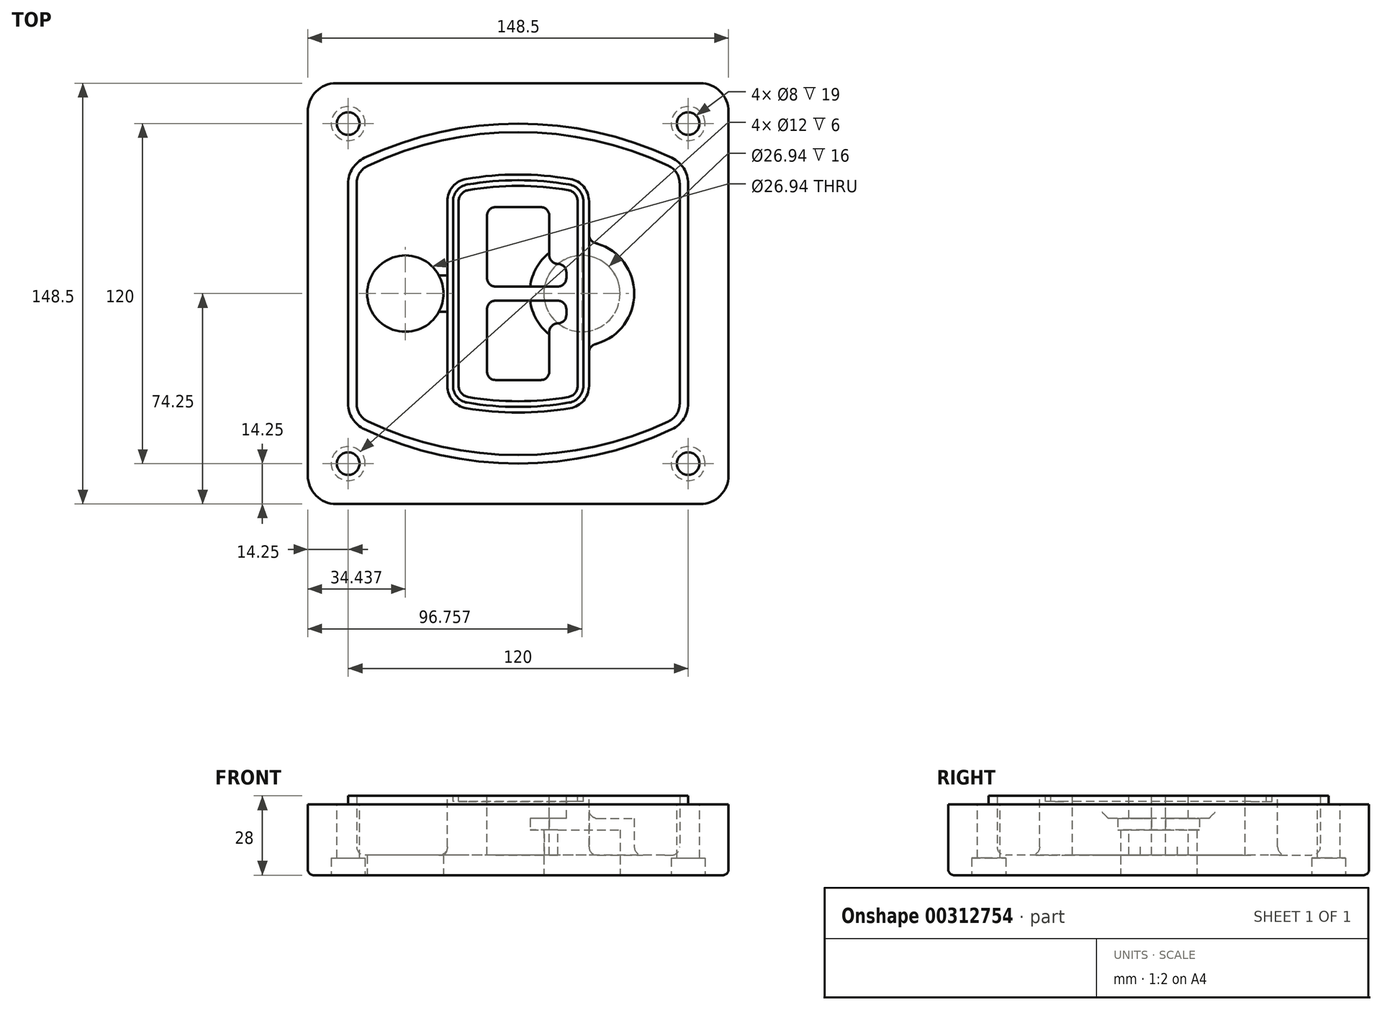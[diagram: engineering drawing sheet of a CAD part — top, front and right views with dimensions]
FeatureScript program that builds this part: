
annotation { "Feature Type Name" : "Feature", "Feature Type Description" : "" }
export const myFeature = defineFeature(function(context is Context, id is Id, definition is map)
    precondition{}
    {
        {
            var Q0;
            Q0=qCreatedBy(makeId("Top.planeOp"),FACE);
            var sketch = newSketch(context, id + "F0", { "sketchPlane" : qUnion([Q0])});
            skPoint(sketch, "E0.rect.middle", {"position": v(0, 0) * mm});
            skLineSegment(sketch, "E1.bottom", {"start": v(-64.25, -74.25) * mm, "end": v(64.25, -74.25) * mm});
            skLineSegment(sketch, "E1.top", {"start": v(-64.25, 74.25) * mm, "end": v(64.25, 74.25) * mm});
            skLineSegment(sketch, "E1.left", {"start": v(-74.25, -64.25) * mm, "end": v(-74.25, 64.25) * mm});
            skLineSegment(sketch, "E1.right", {"start": v(74.25, -64.25) * mm, "end": v(74.25, 64.25) * mm});
            skLineSegment(sketch, "E2", {"start": v(-74.25, 74.25) * mm, "end": v(74.25, -74.25) * mm, "construction": true});
            skLineSegment(sketch, "E3", {"start": v(74.25, 74.25) * mm, "end": v(-74.25, -74.25) * mm, "construction": true});
            skCircle(sketch, "E4", {"center": v(-60, 60) * mm, "radius": 4 * mm});
            skCircle(sketch, "E5", {"center": v(60, 60) * mm, "radius": 4 * mm});
            skCircle(sketch, "E6", {"center": v(60, -60) * mm, "radius": 4 * mm});
            skCircle(sketch, "E7", {"center": v(-60, -60) * mm, "radius": 4 * mm});
            skLineSegment(sketch, "E8", {"start": v(-60, 60) * mm, "end": v(60, 60) * mm, "construction": true});
            skLineSegment(sketch, "E9", {"start": v(60, 60) * mm, "end": v(60, -60) * mm, "construction": true});
            skLineSegment(sketch, "E10", {"start": v(60, -60) * mm, "end": v(-60, -60) * mm, "construction": true});
            skLineSegment(sketch, "E11", {"start": v(-60, -60) * mm, "end": v(-60, 60) * mm, "construction": true});
            skLineSegment(sketch, "E12", {"start": v(-60, 38.83) * mm, "end": v(-60, -38.83) * mm});
            skLineSegment(sketch, "E13", {"start": v(60, 38.83) * mm, "end": v(60, -38.83) * mm});
            skArc(sketch, "E14", {"start": v(54.26, 47.88) * mm, "mid": v(0, 60) * mm, "end": v(-54.26, 47.88) * mm});
            skArc(sketch, "E15", {"start": v(-54.26, -47.88) * mm, "mid": v(0, -60) * mm, "end": v(54.26, -47.88) * mm});
            skLineSegment(sketch, "E16", {"start": v(-60, 0) * mm, "end": v(60, 0) * mm, "construction": true});
            skPoint(sketch, "E17.visualSharp", {"position": v(-60, -45) * mm});
            skArc(sketch, "E17.filletArc", {"start": v(-60, -38.83) * mm, "mid": v(-58.44, -44.2) * mm, "end": v(-54.26, -47.88) * mm});
            skPoint(sketch, "E18.visualSharp", {"position": v(-60, 45) * mm});
            skArc(sketch, "E18.filletArc", {"start": v(-54.26, 47.88) * mm, "mid": v(-58.44, 44.2) * mm, "end": v(-60, 38.83) * mm});
            skPoint(sketch, "E19.visualSharp", {"position": v(60, 45) * mm});
            skArc(sketch, "E19.filletArc", {"start": v(60, 38.83) * mm, "mid": v(58.44, 44.2) * mm, "end": v(54.26, 47.88) * mm});
            skPoint(sketch, "E20.visualSharp", {"position": v(60, -45) * mm});
            skArc(sketch, "E20.filletArc", {"start": v(54.26, -47.88) * mm, "mid": v(58.44, -44.2) * mm, "end": v(60, -38.83) * mm});
            skPoint(sketch, "E21.visualSharp", {"position": v(-74.25, 74.25) * mm});
            skArc(sketch, "E21.filletArc", {"start": v(-64.25, 74.25) * mm, "mid": v(-71.32, 71.32) * mm, "end": v(-74.25, 64.25) * mm});
            skPoint(sketch, "E22.visualSharp", {"position": v(74.25, 74.25) * mm});
            skArc(sketch, "E22.filletArc", {"start": v(74.25, 64.25) * mm, "mid": v(71.32, 71.32) * mm, "end": v(64.25, 74.25) * mm});
            skPoint(sketch, "E23.visualSharp", {"position": v(74.25, -74.25) * mm});
            skArc(sketch, "E23.filletArc", {"start": v(64.25, -74.25) * mm, "mid": v(71.32, -71.32) * mm, "end": v(74.25, -64.25) * mm});
            skPoint(sketch, "E24.visualSharp", {"position": v(-74.25, -74.25) * mm});
            skArc(sketch, "E24.filletArc", {"start": v(-74.25, -64.25) * mm, "mid": v(-71.32, -71.32) * mm, "end": v(-64.25, -74.25) * mm});
            skArc(sketch, "E25.0", {"start": v(57, 38.83) * mm, "mid": v(55.9, 42.58) * mm, "end": v(52.98, 45.17) * mm});
            skLineSegment(sketch, "E25.1", {"start": v(57, 38.83) * mm, "end": v(57, -38.83) * mm});
            skArc(sketch, "E25.2", {"start": v(52.98, -45.17) * mm, "mid": v(55.9, -42.58) * mm, "end": v(57, -38.83) * mm});
            skArc(sketch, "E25.3", {"start": v(-52.98, -45.17) * mm, "mid": v(0, -57) * mm, "end": v(52.98, -45.17) * mm});
            skArc(sketch, "E25.4", {"start": v(-57, -38.83) * mm, "mid": v(-55.9, -42.58) * mm, "end": v(-52.98, -45.17) * mm});
            skArc(sketch, "E25.5", {"start": v(52.98, 45.17) * mm, "mid": v(0, 57) * mm, "end": v(-52.98, 45.17) * mm});
            skLineSegment(sketch, "E25.6", {"start": v(-57, 38.83) * mm, "end": v(-57, -38.83) * mm});
            skArc(sketch, "E25.7", {"start": v(-52.98, 45.17) * mm, "mid": v(-55.9, 42.58) * mm, "end": v(-57, 38.83) * mm});
            skArc(sketch, "E26.0", {"start": v(-55.96, 51.5) * mm, "mid": v(-61.82, 46.33) * mm, "end": v(-64, 38.83) * mm});
            skArc(sketch, "E26.1", {"start": v(55.96, 51.5) * mm, "mid": v(0, 64) * mm, "end": v(-55.96, 51.5) * mm});
            skArc(sketch, "E26.2", {"start": v(64, 38.83) * mm, "mid": v(61.82, 46.33) * mm, "end": v(55.96, 51.5) * mm});
            skLineSegment(sketch, "E26.3", {"start": v(64, 38.83) * mm, "end": v(64, -38.83) * mm});
            skArc(sketch, "E26.4", {"start": v(55.96, -51.5) * mm, "mid": v(61.82, -46.33) * mm, "end": v(64, -38.83) * mm});
            skLineSegment(sketch, "E26.5", {"start": v(-64, 38.83) * mm, "end": v(-64, -38.83) * mm});
            skArc(sketch, "E26.6", {"start": v(-55.96, -51.5) * mm, "mid": v(0, -64) * mm, "end": v(55.96, -51.5) * mm});
            skArc(sketch, "E26.7", {"start": v(-64, -38.83) * mm, "mid": v(-61.82, -46.33) * mm, "end": v(-55.96, -51.5) * mm});
            skLineSegment(sketch, "E27", {"start": v(0, 74.25) * mm, "end": v(0, 104.25) * mm, "construction": true});
            skPoint(sketch, "E27.endSnap0", {"position": v(0, 74.25) * mm});
            skCircle(sketch, "E28", {"center": v(0, 104.25) * mm, "radius": 0.06 * mm});
            skCircle(sketch, "E29", {"center": v(0, 104.25) * mm, "radius": 6 * mm});
            skLineSegment(sketch, "E30", {"start": v(-42.56, 74.25) * mm, "end": v(-18.11, 96.1) * mm});
            skLineSegment(sketch, "E31", {"start": v(11.89, 96.1) * mm, "end": v(31.43, 74.25) * mm});
            skLineSegment(sketch, "E32", {"start": v(-18.11, 96.1) * mm, "end": v(-18.11, 113.16) * mm});
            skLineSegment(sketch, "E33", {"start": v(11.89, 96.1) * mm, "end": v(11.89, 113.16) * mm});
            skArc(sketch, "E34", {"start": v(11.89, 113.16) * mm, "mid": v(-3.11, 128.16) * mm, "end": v(-18.11, 113.16) * mm});
            skSolve(sketch);
        }
        {
            var Q0;
            Q0=makeQuery(id+"F0.imprint","IMPRINT",FACE,{"disambiguationData":[TD([[makeQuery(id+"F0.imprint","IMPRINT",EDGE,{"derivedFrom":sQuery(id+"F0.wireOp",EDGE,"E1.bottom")}),1.0]])]});
            var Q1;
            Q1=makeQuery(id+"F0.imprint","IMPRINT",FACE,{"disambiguationData":[TD([[makeQuery(id+"F0.imprint","IMPRINT",EDGE,{"derivedFrom":sQuery(id+"F0.wireOp",EDGE,"E12")}),1.0]])]});
            var Q2;
            Q2=makeQuery(id+"F0.imprint","IMPRINT",FACE,{"disambiguationData":[TD([[makeQuery(id+"F0.imprint","IMPRINT",EDGE,{"derivedFrom":sQuery(id+"F0.wireOp",EDGE,"E25.0")}),1.0]])]});
            var Q3;
            Q3=makeQuery(id+"F0.imprint","IMPRINT",FACE,{"disambiguationData":[TD([[makeQuery(id+"F0.imprint","IMPRINT",EDGE,{"derivedFrom":sQuery(id+"F0.wireOp",EDGE,"E12")}),-1.0]])]});
            extrude(context, id + "F1", {"entities" : qUnion([Q0, Q1, Q2, Q3]), "oppositeDirection" : true, "depth" : 25 * mm});
        }
        {
            var Q0;
            Q0=makeQuery(id+"F0.imprint","IMPRINT",FACE,{"disambiguationData":[TD([[makeQuery(id+"F0.imprint","IMPRINT",EDGE,{"derivedFrom":sQuery(id+"F0.wireOp",EDGE,"E12")}),1.0]])]});
            extrude(context, id + "F2", {"entities" : qUnion([Q0]), "operationType" : NewBodyOperationType.ADD, "depth" : 3 * mm});
        }
        {
            var Q0;
            Q0=makeQuery(id+"F0.imprint","IMPRINT",FACE,{"disambiguationData":[TD([[makeQuery(id+"F0.imprint","IMPRINT",EDGE,{"derivedFrom":sQuery(id+"F0.wireOp",EDGE,"E25.0")}),1.0]])]});
            extrude(context, id + "F3", {"entities" : qUnion([Q0]), "operationType" : NewBodyOperationType.REMOVE, "oppositeDirection" : true, "depth" : 18 * mm});
        }
        {
            var Q0;
            Q0=makeQuery(id+"F2.opExtrude","CAP_FACE",FACE,{"disambiguationData":[OSD([sQuery(id+"F0.wireOp",EDGE,"E12"),sQuery(id+"F0.wireOp",EDGE,"E13"),sQuery(id+"F0.wireOp",EDGE,"E14"),sQuery(id+"F0.wireOp",EDGE,"E15"),sQuery(id+"F0.wireOp",EDGE,"E17.filletArc"),sQuery(id+"F0.wireOp",EDGE,"E18.filletArc"),sQuery(id+"F0.wireOp",EDGE,"E19.filletArc"),sQuery(id+"F0.wireOp",EDGE,"E20.filletArc"),sQuery(id+"F0.wireOp",EDGE,"E25.0"),sQuery(id+"F0.wireOp",EDGE,"E25.1"),sQuery(id+"F0.wireOp",EDGE,"E25.2"),sQuery(id+"F0.wireOp",EDGE,"E25.3"),sQuery(id+"F0.wireOp",EDGE,"E25.4"),sQuery(id+"F0.wireOp",EDGE,"E25.5"),sQuery(id+"F0.wireOp",EDGE,"E25.6"),sQuery(id+"F0.wireOp",EDGE,"E25.7")])],"isStart":false});
            var sketch = newSketch(context, id + "F4", { "sketchPlane" : qUnion([Q0])});
            skArc(sketch, "E35.0", {"start": v(-18.34, -40.45) * mm, "mid": v(0, -42) * mm, "end": v(18.34, -40.45) * mm});
            skArc(sketch, "E36.0", {"start": v(18.34, 40.45) * mm, "mid": v(0, 42) * mm, "end": v(-18.34, 40.45) * mm});
            skLineSegment(sketch, "E37", {"start": v(-25, 32.57) * mm, "end": v(-25, -32.57) * mm});
            skLineSegment(sketch, "E38", {"start": v(25, 32.57) * mm, "end": v(25, -32.57) * mm});
            skLineSegment(sketch, "E39", {"start": v(-25, 39.1) * mm, "end": v(25, 39.1) * mm, "construction": true});
            skLineSegment(sketch, "E40", {"start": v(-25, -39.1) * mm, "end": v(25, -39.1) * mm, "construction": true});
            skPoint(sketch, "E41.visualSharp", {"position": v(-25, 39.1) * mm});
            skArc(sketch, "E41.filletArc", {"start": v(-18.34, 40.45) * mm, "mid": v(-23.11, 37.73) * mm, "end": v(-25, 32.57) * mm});
            skPoint(sketch, "E42.visualSharp", {"position": v(25, 39.1) * mm});
            skArc(sketch, "E42.filletArc", {"start": v(25, 32.57) * mm, "mid": v(23.11, 37.73) * mm, "end": v(18.34, 40.45) * mm});
            skPoint(sketch, "E43.visualSharp", {"position": v(25, -39.1) * mm});
            skArc(sketch, "E43.filletArc", {"start": v(18.34, -40.45) * mm, "mid": v(23.11, -37.73) * mm, "end": v(25, -32.57) * mm});
            skPoint(sketch, "E44.visualSharp", {"position": v(-25, -39.1) * mm});
            skArc(sketch, "E44.filletArc", {"start": v(-25, -32.57) * mm, "mid": v(-23.11, -37.73) * mm, "end": v(-18.34, -40.45) * mm});
            skArc(sketch, "E45.0", {"start": v(52.98, 45.17) * mm, "mid": v(0, 57) * mm, "end": v(-52.98, 45.17) * mm});
            skArc(sketch, "E45.1", {"start": v(-52.98, 45.17) * mm, "mid": v(-55.9, 42.58) * mm, "end": v(-57, 38.83) * mm});
            skLineSegment(sketch, "E45.2", {"start": v(-57, 38.83) * mm, "end": v(-57, -38.83) * mm});
            skArc(sketch, "E45.3", {"start": v(-57, -38.83) * mm, "mid": v(-55.9, -42.58) * mm, "end": v(-52.98, -45.17) * mm});
            skArc(sketch, "E45.4", {"start": v(-52.98, -45.17) * mm, "mid": v(0, -57) * mm, "end": v(52.98, -45.17) * mm});
            skArc(sketch, "E45.5", {"start": v(52.98, -45.17) * mm, "mid": v(55.9, -42.58) * mm, "end": v(57, -38.83) * mm});
            skLineSegment(sketch, "E45.6", {"start": v(57, 38.83) * mm, "end": v(57, -38.83) * mm});
            skArc(sketch, "E45.7", {"start": v(57, 38.83) * mm, "mid": v(55.9, 42.58) * mm, "end": v(52.98, 45.17) * mm});
            skLineSegment(sketch, "E46.0", {"start": v(23, 32.57) * mm, "end": v(23, -32.57) * mm});
            skArc(sketch, "E46.1", {"start": v(18, -38.48) * mm, "mid": v(21.58, -36.44) * mm, "end": v(23, -32.57) * mm});
            skArc(sketch, "E46.2", {"start": v(-18, -38.48) * mm, "mid": v(0, -40) * mm, "end": v(18, -38.48) * mm});
            skArc(sketch, "E46.3", {"start": v(-23, -32.57) * mm, "mid": v(-21.58, -36.44) * mm, "end": v(-18, -38.48) * mm});
            skLineSegment(sketch, "E46.4", {"start": v(-23, 32.57) * mm, "end": v(-23, -32.57) * mm});
            skArc(sketch, "E46.5", {"start": v(23, 32.57) * mm, "mid": v(21.58, 36.44) * mm, "end": v(18, 38.48) * mm});
            skArc(sketch, "E46.6", {"start": v(-18, 38.48) * mm, "mid": v(-21.58, 36.44) * mm, "end": v(-23, 32.57) * mm});
            skArc(sketch, "E46.7", {"start": v(18, 38.48) * mm, "mid": v(0, 40) * mm, "end": v(-18, 38.48) * mm});
            skArc(sketch, "E47.0", {"start": v(21, 32.57) * mm, "mid": v(20.06, 35.15) * mm, "end": v(17.67, 36.5) * mm});
            skLineSegment(sketch, "E47.1", {"start": v(21, 32.57) * mm, "end": v(21, -32.57) * mm});
            skArc(sketch, "E47.2", {"start": v(17.67, -36.5) * mm, "mid": v(20.06, -35.15) * mm, "end": v(21, -32.57) * mm});
            skArc(sketch, "E47.3", {"start": v(-17.67, -36.5) * mm, "mid": v(0, -38) * mm, "end": v(17.67, -36.5) * mm});
            skArc(sketch, "E47.4", {"start": v(-21, -32.57) * mm, "mid": v(-20.06, -35.15) * mm, "end": v(-17.67, -36.5) * mm});
            skArc(sketch, "E47.5", {"start": v(17.67, 36.5) * mm, "mid": v(0, 38) * mm, "end": v(-17.67, 36.5) * mm});
            skLineSegment(sketch, "E47.6", {"start": v(-21, 32.57) * mm, "end": v(-21, -32.57) * mm});
            skArc(sketch, "E47.7", {"start": v(-17.67, 36.5) * mm, "mid": v(-20.06, 35.15) * mm, "end": v(-21, 32.57) * mm});
            skLineSegment(sketch, "E48", {"start": v(-25, 0) * mm, "end": v(25, 0) * mm, "construction": true});
            skLineSegment(sketch, "E49", {"start": v(-11, 5.5) * mm, "end": v(-11, 27.5) * mm});
            skLineSegment(sketch, "E50", {"start": v(-8, 30.5) * mm, "end": v(8, 30.5) * mm});
            skLineSegment(sketch, "E51", {"start": v(11, 27.5) * mm, "end": v(11, 13.5) * mm});
            skLineSegment(sketch, "E52", {"start": v(14, 10.5) * mm, "end": v(14, 10.5) * mm});
            skLineSegment(sketch, "E53", {"start": v(17, 7.5) * mm, "end": v(17, 5.5) * mm});
            skLineSegment(sketch, "E54", {"start": v(14, 2.5) * mm, "end": v(-8, 2.5) * mm});
            skPoint(sketch, "E55.visualSharp", {"position": v(-11, 30.5) * mm});
            skArc(sketch, "E55.filletArc", {"start": v(-8, 30.5) * mm, "mid": v(-10.12, 29.62) * mm, "end": v(-11, 27.5) * mm});
            skPoint(sketch, "E56.visualSharp", {"position": v(11, 30.5) * mm});
            skArc(sketch, "E56.filletArc", {"start": v(11, 27.5) * mm, "mid": v(10.12, 29.62) * mm, "end": v(8, 30.5) * mm});
            skPoint(sketch, "E57.visualSharp", {"position": v(11, 10.5) * mm});
            skArc(sketch, "E57.filletArc", {"start": v(11, 13.5) * mm, "mid": v(11.88, 11.38) * mm, "end": v(14, 10.5) * mm});
            skPoint(sketch, "E58.visualSharp", {"position": v(17, 10.5) * mm});
            skArc(sketch, "E58.filletArc", {"start": v(17, 7.5) * mm, "mid": v(16.12, 9.62) * mm, "end": v(14, 10.5) * mm});
            skPoint(sketch, "E59.visualSharp", {"position": v(17, 2.5) * mm});
            skArc(sketch, "E59.filletArc", {"start": v(14, 2.5) * mm, "mid": v(16.12, 3.38) * mm, "end": v(17, 5.5) * mm});
            skPoint(sketch, "E60.visualSharp", {"position": v(-11, 2.5) * mm});
            skArc(sketch, "E60.filletArc", {"start": v(-11, 5.5) * mm, "mid": v(-10.12, 3.38) * mm, "end": v(-8, 2.5) * mm});
            skLineSegment(sketch, "E61.0.MirrorCS", {"start": v(14, -2.5) * mm, "end": v(-8, -2.5) * mm});
            skArc(sketch, "E62.0.MirrorCS", {"start": v(-11, -5.5) * mm, "mid": v(-10.12, -3.38) * mm, "end": v(-8, -2.5) * mm});
            skLineSegment(sketch, "E63.0.MirrorCS", {"start": v(-11, -5.5) * mm, "end": v(-11, -27.5) * mm});
            skArc(sketch, "E64.0.MirrorCS", {"start": v(-8, -30.5) * mm, "mid": v(-10.12, -29.62) * mm, "end": v(-11, -27.5) * mm});
            skLineSegment(sketch, "E65.0.MirrorCS", {"start": v(-8, -30.5) * mm, "end": v(8, -30.5) * mm});
            skArc(sketch, "E66.0.MirrorCS", {"start": v(11, -27.5) * mm, "mid": v(10.12, -29.62) * mm, "end": v(8, -30.5) * mm});
            skLineSegment(sketch, "E67.0.MirrorCS", {"start": v(11, -27.5) * mm, "end": v(11, -13.5) * mm});
            skArc(sketch, "E68.0.MirrorCS", {"start": v(11, -13.5) * mm, "mid": v(11.88, -11.38) * mm, "end": v(14, -10.5) * mm});
            skArc(sketch, "E69.0.MirrorCS", {"start": v(17, -7.5) * mm, "mid": v(16.12, -9.62) * mm, "end": v(14, -10.5) * mm});
            skLineSegment(sketch, "E70.0.MirrorCS", {"start": v(17, -7.5) * mm, "end": v(17, -5.5) * mm});
            skArc(sketch, "E71.0.MirrorCS", {"start": v(14, -2.5) * mm, "mid": v(16.12, -3.38) * mm, "end": v(17, -5.5) * mm});
            skSolve(sketch);
        }
        {
            var Q0;
            Q0=makeQuery(id+"F4.imprint","IMPRINT",FACE,{"disambiguationData":[TD([[makeQuery(id+"F4.imprint","IMPRINT",EDGE,{"derivedFrom":sQuery(id+"F4.wireOp",EDGE,"E35.0")}),1.0]])]});
            var Q1;
            Q1=makeQuery(id+"F4.imprint","IMPRINT",FACE,{"disambiguationData":[TD([[makeQuery(id+"F4.imprint","IMPRINT",EDGE,{"derivedFrom":sQuery(id+"F4.wireOp",EDGE,"E46.0")}),-1.0]])]});
            var Q2;
            Q2=makeQuery(id+"F4.imprint","IMPRINT",FACE,{"disambiguationData":[TD([[makeQuery(id+"F4.imprint","IMPRINT",EDGE,{"derivedFrom":sQuery(id+"F4.wireOp",EDGE,"E47.0")}),1.0]])]});
            extrude(context, id + "F5", {"entities" : qUnion([Q0, Q1, Q2]), "operationType" : NewBodyOperationType.ADD, "endBound" : BoundingType.UP_TO_NEXT, "oppositeDirection" : true, "depth" : 25 * mm});
        }
        {
            var Q0;
            Q0=makeQuery(id+"F4.imprint","IMPRINT",FACE,{"disambiguationData":[TD([[makeQuery(id+"F4.imprint","IMPRINT",EDGE,{"derivedFrom":sQuery(id+"F4.wireOp",EDGE,"E46.0")}),-1.0]])]});
            extrude(context, id + "F6", {"entities" : qUnion([Q0]), "operationType" : NewBodyOperationType.REMOVE, "oppositeDirection" : true, "depth" : 2 * mm});
        }
        {
            var Q0;
            Q0=makeQuery(id+"F1.opExtrude","CAP_FACE",FACE,{"disambiguationData":[OSD([sQuery(id+"F0.wireOp",EDGE,"E1.bottom"),sQuery(id+"F0.wireOp",EDGE,"E1.top"),sQuery(id+"F0.wireOp",EDGE,"E1.left"),sQuery(id+"F0.wireOp",EDGE,"E1.right"),sQuery(id+"F0.wireOp",EDGE,"E4"),sQuery(id+"F0.wireOp",EDGE,"E5"),sQuery(id+"F0.wireOp",EDGE,"E6"),sQuery(id+"F0.wireOp",EDGE,"E7"),sQuery(id+"F0.wireOp",EDGE,"E21.filletArc"),sQuery(id+"F0.wireOp",EDGE,"E22.filletArc"),sQuery(id+"F0.wireOp",EDGE,"E23.filletArc"),sQuery(id+"F0.wireOp",EDGE,"E24.filletArc")])],"isStart":false});
            var sketch = newSketch(context, id + "F7", { "sketchPlane" : qUnion([Q0])});
            skCircle(sketch, "E72", {"center": v(22.5, 0) * mm, "radius": 13.47 * mm});
            skCircle(sketch, "E73", {"center": v(-39.81, 0) * mm, "radius": 13.47 * mm});
            skLineSegment(sketch, "E74", {"start": v(74.25, 0) * mm, "end": v(-74.25, 0) * mm});
            skCircle(sketch, "E75", {"center": v(22.5, 0) * mm, "radius": 18.47 * mm});
            skCircle(sketch, "E76", {"center": v(60, -60) * mm, "radius": 6 * mm});
            skCircle(sketch, "E77", {"center": v(-60, -60) * mm, "radius": 6 * mm});
            skCircle(sketch, "E78", {"center": v(-60, 60) * mm, "radius": 6 * mm});
            skCircle(sketch, "E79", {"center": v(60, 60) * mm, "radius": 6 * mm});
            skSolve(sketch);
        }
        {
            var Q0;
            {var subQ1=sQuery(id+"F7.wireOp",EDGE,"E74");var subQ4=sQuery(id+"F7.wireOp",EDGE,"E72");var subQ6=makeQuery(id+"F7.imprint","INTERSECT",VERTEX,{"disambiguationData":[OD(0.0)],"derivedFrom":[subQ4,subQ1]});Q0=makeQuery(id+"F7.imprint","IMPRINT",FACE,{"disambiguationData":[TD([[makeQuery(id+"F7.imprint","IMPRINT",EDGE,{"disambiguationData":[TD([[subQ6,-1.0]])],"derivedFrom":subQ4}),-1.0]])]});}
            var Q1;
            {var subQ0=sQuery(id+"F7.wireOp",EDGE,"E74");var subQ1=sQuery(id+"F7.wireOp",EDGE,"E72");var subQ3=makeQuery(id+"F7.imprint","INTERSECT",VERTEX,{"disambiguationData":[OD(0.0)],"derivedFrom":[subQ1,subQ0]});Q1=makeQuery(id+"F7.imprint","IMPRINT",FACE,{"disambiguationData":[TD([[makeQuery(id+"F7.imprint","IMPRINT",EDGE,{"disambiguationData":[TD([[subQ3,-1.0]])],"derivedFrom":subQ1}),1.0]])]});}
            var Q2;
            {var subQ0=sQuery(id+"F7.wireOp",EDGE,"E74");var subQ1=sQuery(id+"F7.wireOp",EDGE,"E72");var subQ3=makeQuery(id+"F7.imprint","INTERSECT",VERTEX,{"disambiguationData":[OD(0.0)],"derivedFrom":[subQ1,subQ0]});Q2=makeQuery(id+"F7.imprint","IMPRINT",FACE,{"disambiguationData":[TD([[makeQuery(id+"F7.imprint","IMPRINT",EDGE,{"disambiguationData":[TD([[subQ3,1.0]])],"derivedFrom":subQ1}),1.0]])]});}
            var Q3;
            {var subQ1=sQuery(id+"F7.wireOp",EDGE,"E74");var subQ4=sQuery(id+"F7.wireOp",EDGE,"E72");var subQ6=makeQuery(id+"F7.imprint","INTERSECT",VERTEX,{"disambiguationData":[OD(0.0)],"derivedFrom":[subQ4,subQ1]});Q3=makeQuery(id+"F7.imprint","IMPRINT",FACE,{"disambiguationData":[TD([[makeQuery(id+"F7.imprint","IMPRINT",EDGE,{"disambiguationData":[TD([[subQ6,1.0]])],"derivedFrom":subQ4}),-1.0]])]});}
            extrude(context, id + "F8", {"entities" : qUnion([Q0, Q1, Q2, Q3]), "operationType" : NewBodyOperationType.ADD, "oppositeDirection" : true, "depth" : 20 * mm});
        }
        {
            var Q0;
            {var subQ0=sQuery(id+"F7.wireOp",EDGE,"E74");var subQ1=sQuery(id+"F7.wireOp",EDGE,"E72");var subQ3=makeQuery(id+"F7.imprint","INTERSECT",VERTEX,{"disambiguationData":[OD(0.0)],"derivedFrom":[subQ1,subQ0]});Q0=makeQuery(id+"F7.imprint","IMPRINT",FACE,{"disambiguationData":[TD([[makeQuery(id+"F7.imprint","IMPRINT",EDGE,{"disambiguationData":[TD([[subQ3,-1.0]])],"derivedFrom":subQ1}),1.0]])]});}
            var Q1;
            {var subQ0=sQuery(id+"F7.wireOp",EDGE,"E74");var subQ1=sQuery(id+"F7.wireOp",EDGE,"E72");var subQ3=makeQuery(id+"F7.imprint","INTERSECT",VERTEX,{"disambiguationData":[OD(0.0)],"derivedFrom":[subQ1,subQ0]});Q1=makeQuery(id+"F7.imprint","IMPRINT",FACE,{"disambiguationData":[TD([[makeQuery(id+"F7.imprint","IMPRINT",EDGE,{"disambiguationData":[TD([[subQ3,1.0]])],"derivedFrom":subQ1}),1.0]])]});}
            extrude(context, id + "F9", {"entities" : qUnion([Q0, Q1]), "operationType" : NewBodyOperationType.REMOVE, "oppositeDirection" : true, "depth" : 16 * mm});
        }
        {
            var Q0;
            {var subQ0=sQuery(id+"F7.wireOp",EDGE,"E74");var subQ1=sQuery(id+"F7.wireOp",EDGE,"E73");var subQ3=makeQuery(id+"F7.imprint","INTERSECT",VERTEX,{"disambiguationData":[OD(0.0)],"derivedFrom":[subQ1,subQ0]});Q0=makeQuery(id+"F7.imprint","IMPRINT",FACE,{"disambiguationData":[TD([[makeQuery(id+"F7.imprint","IMPRINT",EDGE,{"disambiguationData":[TD([[subQ3,-1.0]])],"derivedFrom":subQ1}),1.0]])]});}
            var Q1;
            {var subQ0=sQuery(id+"F7.wireOp",EDGE,"E74");var subQ1=sQuery(id+"F7.wireOp",EDGE,"E73");var subQ3=makeQuery(id+"F7.imprint","INTERSECT",VERTEX,{"disambiguationData":[OD(0.0)],"derivedFrom":[subQ1,subQ0]});Q1=makeQuery(id+"F7.imprint","IMPRINT",FACE,{"disambiguationData":[TD([[makeQuery(id+"F7.imprint","IMPRINT",EDGE,{"disambiguationData":[TD([[subQ3,1.0]])],"derivedFrom":subQ1}),1.0]])]});}
            extrude(context, id + "F10", {"entities" : qUnion([Q0, Q1]), "operationType" : NewBodyOperationType.REMOVE, "oppositeDirection" : true, "depth" : 25 * mm});
        }
        {
            var Q0;
            Q0=makeQuery(id+"F7.imprint","IMPRINT",FACE,{"disambiguationData":[TD([[makeQuery(id+"F7.imprint","IMPRINT",EDGE,{"derivedFrom":sQuery(id+"F7.wireOp",EDGE,"E76")}),1.0]])]});
            var Q1;
            Q1=makeQuery(id+"F7.imprint","IMPRINT",FACE,{"disambiguationData":[TD([[makeQuery(id+"F7.imprint","IMPRINT",EDGE,{"derivedFrom":makeQuery(id+"F1.opExtrude","CAP_EDGE",EDGE,{"disambiguationData":[OSD([sQuery(id+"F0.wireOp",EDGE,"E5")])],"isStart":false})}),-1.0]])]});
            var Q2;
            Q2=makeQuery(id+"F7.imprint","IMPRINT",FACE,{"disambiguationData":[TD([[makeQuery(id+"F7.imprint","IMPRINT",EDGE,{"derivedFrom":sQuery(id+"F7.wireOp",EDGE,"E77")}),1.0]])]});
            var Q3;
            Q3=makeQuery(id+"F7.imprint","IMPRINT",FACE,{"disambiguationData":[TD([[makeQuery(id+"F7.imprint","IMPRINT",EDGE,{"derivedFrom":makeQuery(id+"F1.opExtrude","CAP_EDGE",EDGE,{"disambiguationData":[OSD([sQuery(id+"F0.wireOp",EDGE,"E4")])],"isStart":false})}),-1.0]])]});
            var Q4;
            Q4=makeQuery(id+"F7.imprint","IMPRINT",FACE,{"disambiguationData":[TD([[makeQuery(id+"F7.imprint","IMPRINT",EDGE,{"derivedFrom":sQuery(id+"F7.wireOp",EDGE,"E78")}),1.0]])]});
            var Q5;
            Q5=makeQuery(id+"F7.imprint","IMPRINT",FACE,{"disambiguationData":[TD([[makeQuery(id+"F7.imprint","IMPRINT",EDGE,{"derivedFrom":makeQuery(id+"F1.opExtrude","CAP_EDGE",EDGE,{"disambiguationData":[OSD([sQuery(id+"F0.wireOp",EDGE,"E7")])],"isStart":false})}),-1.0]])]});
            var Q6;
            Q6=makeQuery(id+"F7.imprint","IMPRINT",FACE,{"disambiguationData":[TD([[makeQuery(id+"F7.imprint","IMPRINT",EDGE,{"derivedFrom":sQuery(id+"F7.wireOp",EDGE,"E79")}),1.0]])]});
            var Q7;
            Q7=makeQuery(id+"F7.imprint","IMPRINT",FACE,{"disambiguationData":[TD([[makeQuery(id+"F7.imprint","IMPRINT",EDGE,{"derivedFrom":makeQuery(id+"F1.opExtrude","CAP_EDGE",EDGE,{"disambiguationData":[OSD([sQuery(id+"F0.wireOp",EDGE,"E6")])],"isStart":false})}),-1.0]])]});
            extrude(context, id + "F11", {"entities" : qUnion([Q0, Q1, Q2, Q3, Q4, Q5, Q6, Q7]), "operationType" : NewBodyOperationType.REMOVE, "oppositeDirection" : true, "depth" : 6 * mm});
        }
        {
            var Q0;
            Q0=makeQuery(id+"F9.boolean.opBoolean","COPY",FACE,{"derivedFrom":makeQuery(id+"F9.opExtrude","CAP_FACE",FACE,{"disambiguationData":[OSD([sQuery(id+"F7.wireOp",EDGE,"E72")])],"isStart":false})});
            var sketch = newSketch(context, id + "F12", { "sketchPlane" : qUnion([Q0])});
            skArc(sketch, "E80.0", {"start": v(11, 14.45) * mm, "mid": v(6.45, 9.13) * mm, "end": v(4.2, 2.5) * mm});
            skArc(sketch, "E80.1", {"start": v(4.2, -2.5) * mm, "mid": v(6.45, -9.13) * mm, "end": v(11, -14.45) * mm});
            skLineSegment(sketch, "E81", {"start": v(4.2, -2.5) * mm, "end": v(14, -2.5) * mm});
            skLineSegment(sketch, "E82.0", {"start": v(14, 2.5) * mm, "end": v(4.2, 2.5) * mm});
            skArc(sketch, "E82.1", {"start": v(14, 2.5) * mm, "mid": v(16.12, 3.38) * mm, "end": v(17, 5.5) * mm});
            skLineSegment(sketch, "E82.2", {"start": v(17, 7.5) * mm, "end": v(17, 5.5) * mm});
            skArc(sketch, "E82.3", {"start": v(17, 7.5) * mm, "mid": v(16.12, 9.62) * mm, "end": v(14, 10.5) * mm});
            skArc(sketch, "E82.4", {"start": v(11, 13.5) * mm, "mid": v(11.88, 11.38) * mm, "end": v(14, 10.5) * mm});
            skLineSegment(sketch, "E82.5", {"start": v(11, 14.45) * mm, "end": v(11, 13.5) * mm});
            skLineSegment(sketch, "E82.7", {"start": v(14, -2.5) * mm, "end": v(4.2, -2.5) * mm});
            skArc(sketch, "E82.8", {"start": v(14, -2.5) * mm, "mid": v(16.12, -3.38) * mm, "end": v(17, -5.5) * mm});
            skLineSegment(sketch, "E82.9", {"start": v(17, -7.5) * mm, "end": v(17, -5.5) * mm});
            skArc(sketch, "E82.10", {"start": v(17, -7.5) * mm, "mid": v(16.12, -9.62) * mm, "end": v(14, -10.5) * mm});
            skArc(sketch, "E82.11", {"start": v(11, -13.5) * mm, "mid": v(11.88, -11.38) * mm, "end": v(14, -10.5) * mm});
            skLineSegment(sketch, "E82.12", {"start": v(11, -14.45) * mm, "end": v(11, -13.5) * mm});
            skPoint(sketch, "E83.orphan", {"position": v(11, -27.5) * mm});
            skPoint(sketch, "E84.orphan", {"position": v(-8, -2.5) * mm});
            skPoint(sketch, "E85.orphan", {"position": v(-8, 2.5) * mm});
            skPoint(sketch, "E86.orphan", {"position": v(11, 27.5) * mm});
            skSolve(sketch);
        }
        {
            var Q0;
            {var subQ7=sQuery(id+"F12.wireOp",EDGE,"E80.0");var subQ14=sQuery(id+"F12.wireOp",EDGE,"E80.1");var subQ16=sQuery(id+"F12.wireOp",EDGE,"E82.1");var subQ18=sQuery(id+"F12.wireOp",EDGE,"E82.8");Q0=qUnion([makeQuery(id+"F12.imprint","IMPRINT",FACE,{"disambiguationData":[TD([[makeQuery(id+"F12.imprint","IMPRINT",EDGE,{"derivedFrom":subQ7}),1.0]])]}),makeQuery(id+"F12.imprint","IMPRINT",FACE,{"disambiguationData":[TD([[makeQuery(id+"F12.imprint","IMPRINT",EDGE,{"derivedFrom":subQ14}),1.0]])]}),makeQuery(id+"F12.imprint","IMPRINT",FACE,{"disambiguationData":[TD([[makeQuery(id+"F12.imprint","IMPRINT",EDGE,{"derivedFrom":subQ16}),1.0]])]}),makeQuery(id+"F12.imprint","IMPRINT",FACE,{"disambiguationData":[TD([[makeQuery(id+"F12.imprint","IMPRINT",EDGE,{"derivedFrom":subQ18}),-1.0]])]})]);}
            var Q1;
            Q1=makeQuery(id+"F5.boolean.opBoolean","SPLIT",FACE,{"disambiguationData":[TD([makeQuery(id+"F5.opExtrude","SWEPT_FACE",FACE,{"disambiguationData":[OSD([sQuery(id+"F4.wireOp",EDGE,"E49")])]})])],"derivedFrom":makeQuery(id+"F3.boolean.opBoolean","COPY",FACE,{"derivedFrom":makeQuery(id+"F3.opExtrude","CAP_FACE",FACE,{"disambiguationData":[OSD([sQuery(id+"F0.wireOp",EDGE,"E25.0"),sQuery(id+"F0.wireOp",EDGE,"E25.1"),sQuery(id+"F0.wireOp",EDGE,"E25.2"),sQuery(id+"F0.wireOp",EDGE,"E25.3"),sQuery(id+"F0.wireOp",EDGE,"E25.4"),sQuery(id+"F0.wireOp",EDGE,"E25.5"),sQuery(id+"F0.wireOp",EDGE,"E25.6"),sQuery(id+"F0.wireOp",EDGE,"E25.7")])],"isStart":false})})});
            extrude(context, id + "F13", {"entities" : qUnion([Q0]), "operationType" : NewBodyOperationType.REMOVE, "endBound" : BoundingType.UP_TO_SURFACE, "endBoundEntityFace" : qUnion([Q1]), "depth" : 25 * mm});
        }
        {
            var Q0;
            Q0=makeQuery(id+"F3.boolean.opBoolean","COPY",EDGE,{"derivedFrom":makeQuery(id+"F3.opExtrude","CAP_EDGE",EDGE,{"disambiguationData":[OSD([sQuery(id+"F0.wireOp",EDGE,"E25.6")])],"isStart":false})});
            var Q1;
            Q1=makeQuery(id+"F8.boolean.opBoolean","INTERSECT",EDGE,{"derivedFrom":[makeQuery(id+"F5.opExtrude","SWEPT_FACE",FACE,{"disambiguationData":[OSD([sQuery(id+"F4.wireOp",EDGE,"E38")])]}),makeQuery(id+"F8.opExtrude","CAP_FACE",FACE,{"disambiguationData":[OSD([sQuery(id+"F7.wireOp",EDGE,"E75")])],"isStart":false})]});
            var Q2;
            Q2=makeQuery(id+"F8.boolean.opBoolean","INTERSECT",EDGE,{"disambiguationData":[OD(1.0)],"derivedFrom":[makeQuery(id+"F5.opExtrude","SWEPT_FACE",FACE,{"disambiguationData":[OSD([sQuery(id+"F4.wireOp",EDGE,"E38")])]}),makeQuery(id+"F8.opExtrude","SWEPT_FACE",FACE,{"disambiguationData":[OSD([sQuery(id+"F7.wireOp",EDGE,"E75")])]})]});
            var Q3;
            {var subQ0=sQuery(id+"F4.wireOp",EDGE,"E38");Q3=makeQuery(id+"F8.boolean.opBoolean","SPLIT",EDGE,{"disambiguationData":[TD([makeQuery(id+"F5.opExtrude","SWEPT_FACE",FACE,{"disambiguationData":[OSD([sQuery(id+"F4.wireOp",EDGE,"E43.filletArc")])]})])],"derivedFrom":makeQuery(id+"F5.opExtrude","CAP_EDGE",EDGE,{"disambiguationData":[OSD([subQ0])],"isStart":false})});}
            var Q4;
            {var subQ0=sQuery(id+"F0.wireOp",EDGE,"E25.7");var subQ1=sQuery(id+"F0.wireOp",EDGE,"E25.1");var subQ2=sQuery(id+"F0.wireOp",EDGE,"E25.6");var subQ3=sQuery(id+"F0.wireOp",EDGE,"E25.5");var subQ4=sQuery(id+"F0.wireOp",EDGE,"E25.4");var subQ5=sQuery(id+"F0.wireOp",EDGE,"E25.0");var subQ6=sQuery(id+"F0.wireOp",EDGE,"E25.2");var subQ7=sQuery(id+"F0.wireOp",EDGE,"E25.3");Q4=makeQuery(id+"F8.boolean.opBoolean","INTERSECT",EDGE,{"derivedFrom":[makeQuery(id+"F5.boolean.opBoolean","SPLIT",FACE,{"disambiguationData":[TD([makeQuery(id+"F2.opExtrude","SWEPT_FACE",FACE,{"disambiguationData":[OSD([subQ5])]})])],"derivedFrom":makeQuery(id+"F3.boolean.opBoolean","COPY",FACE,{"derivedFrom":makeQuery(id+"F3.opExtrude","CAP_FACE",FACE,{"disambiguationData":[OSD([subQ5,subQ1,subQ6,subQ7,subQ4,subQ3,subQ2,subQ0])],"isStart":false})})}),makeQuery(id+"F8.opExtrude","SWEPT_FACE",FACE,{"disambiguationData":[OSD([sQuery(id+"F7.wireOp",EDGE,"E75")])]})]});}
            var Q5;
            Q5=makeQuery(id+"F8.boolean.opBoolean","INTERSECT",EDGE,{"disambiguationData":[OD(0.0)],"derivedFrom":[makeQuery(id+"F5.opExtrude","SWEPT_FACE",FACE,{"disambiguationData":[OSD([sQuery(id+"F4.wireOp",EDGE,"E38")])]}),makeQuery(id+"F8.opExtrude","SWEPT_FACE",FACE,{"disambiguationData":[OSD([sQuery(id+"F7.wireOp",EDGE,"E75")])]})]});
            fillet(context, id + "F14", {"entities" : qUnion([Q0, Q1, Q2, Q3, Q4, Q5]), "radius" : 3 * mm, "tangentPropagation" : true, "allowEdgeOverflow" : false});
        }
        {
            var Q0;
            Q0=makeQuery(id+"F1.opExtrude","CAP_EDGE",EDGE,{"disambiguationData":[OSD([sQuery(id+"F0.wireOp",EDGE,"E1.bottom")])],"isStart":false});
            fillet(context, id + "F15", {"entities" : qUnion([Q0]), "radius" : 2 * mm, "tangentPropagation" : true, "allowEdgeOverflow" : false});
        }
    });
